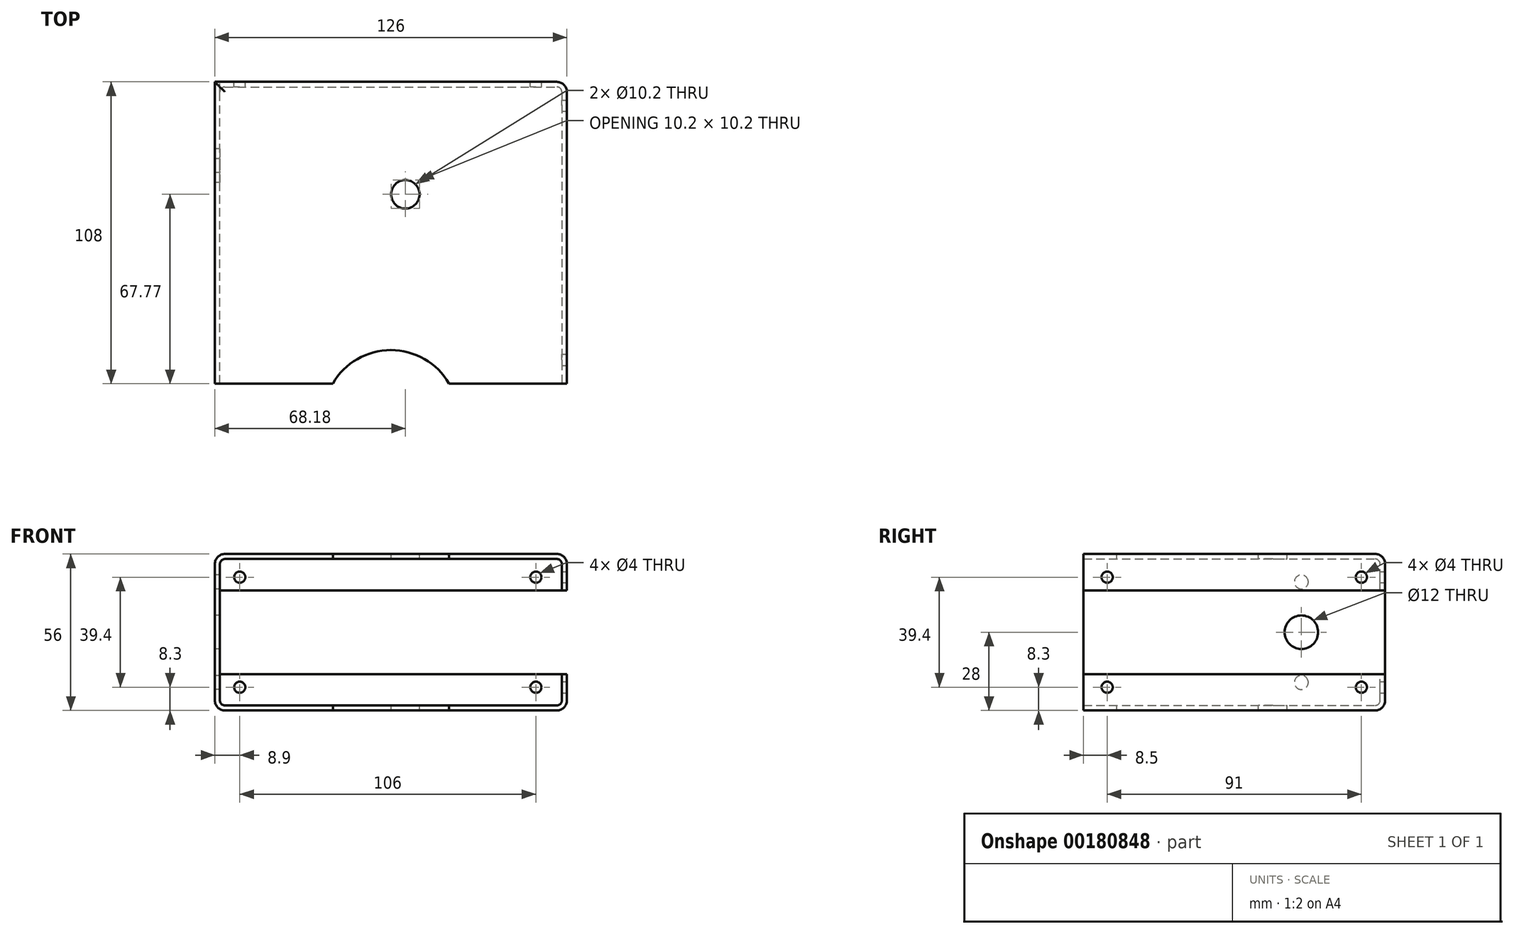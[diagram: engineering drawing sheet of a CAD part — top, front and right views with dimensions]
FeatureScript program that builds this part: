
annotation { "Feature Type Name" : "Feature", "Feature Type Description" : "" }
export const myFeature = defineFeature(function(context is Context, id is Id, definition is map)
    precondition{}
    {
        {
            var Q0;
            Q0=qCreatedBy(makeId("Front.planeOp"),FACE);
            var sketch = newSketch(context, id + "F0", { "sketchPlane" : qUnion([Q0])});
            skLineSegment(sketch, "E0.bottom", {"start": v(63, -28) * mm, "end": v(-63, -28) * mm});
            skLineSegment(sketch, "E0.top", {"start": v(63, 28) * mm, "end": v(-63, 28) * mm});
            skLineSegment(sketch, "E0.left", {"start": v(63, -28) * mm, "end": v(63, 28) * mm});
            skLineSegment(sketch, "E0.right", {"start": v(-63, -28) * mm, "end": v(-63, 28) * mm});
            skPoint(sketch, "E0.middle", {"position": v(0, 0) * mm});
            skSolve(sketch);
        }
        {
            var Q0;
            Q0 = qSketchRegion(id + "F0", true);
            extrude(context, id + "F1", {"entities" : qUnion([Q0]), "depth" : 108 * mm});
        }
        {
            var Q0;
            Q0=makeQuery(id+"F1.opExtrude","CAP_FACE",FACE,{"disambiguationData":[OSD([sQuery(id+"F0.wireOp",EDGE,"E0.bottom"),sQuery(id+"F0.wireOp",EDGE,"E0.top"),sQuery(id+"F0.wireOp",EDGE,"E0.left"),sQuery(id+"F0.wireOp",EDGE,"E0.right")])],"isStart":false});
            shell(context, id + "F2", {"entities" : qUnion([Q0]), "thickness" : 1.8 * mm});
        }
        {
            var Q0;
            {var subQ0=sQuery(id+"F0.wireOp",EDGE,"E0.right");Q0=makeQuery(id+"F2.opShell","OFFSET_EDGE",EDGE,{"disambiguationData":[OSD([subQ0]),TDD([makeQuery(id+"F1.opExtrude","CAP_EDGE",EDGE,{"disambiguationData":[OSD([subQ0])],"isStart":true})])]});}
            var Q1;
            Q1=makeQuery(id+"F2.opShell","OFFSET_EDGE",EDGE,{"disambiguationData":[OSD([sQuery(id+"F0.wireOp",EDGE,"E0.bottom"),sQuery(id+"F0.wireOp",EDGE,"E0.right")])]});
            var Q2;
            {var subQ0=sQuery(id+"F0.wireOp",EDGE,"E0.bottom");Q2=makeQuery(id+"F2.opShell","OFFSET_EDGE",EDGE,{"disambiguationData":[OSD([subQ0]),TDD([makeQuery(id+"F1.opExtrude","CAP_EDGE",EDGE,{"disambiguationData":[OSD([subQ0])],"isStart":true})])]});}
            var Q3;
            {var subQ0=sQuery(id+"F0.wireOp",EDGE,"E0.top");Q3=makeQuery(id+"F2.opShell","OFFSET_EDGE",EDGE,{"disambiguationData":[OSD([subQ0]),TDD([makeQuery(id+"F1.opExtrude","CAP_EDGE",EDGE,{"disambiguationData":[OSD([subQ0])],"isStart":true})])]});}
            var Q4;
            Q4=makeQuery(id+"F2.opShell","OFFSET_EDGE",EDGE,{"disambiguationData":[OSD([sQuery(id+"F0.wireOp",EDGE,"E0.top"),sQuery(id+"F0.wireOp",EDGE,"E0.right")])]});
            var Q5;
            {var subQ0=sQuery(id+"F0.wireOp",EDGE,"E0.left");Q5=makeQuery(id+"F2.opShell","OFFSET_EDGE",EDGE,{"disambiguationData":[OSD([subQ0]),TDD([makeQuery(id+"F1.opExtrude","CAP_EDGE",EDGE,{"disambiguationData":[OSD([subQ0])],"isStart":true})])]});}
            var Q6;
            Q6=makeQuery(id+"F2.opShell","OFFSET_EDGE",EDGE,{"disambiguationData":[OSD([sQuery(id+"F0.wireOp",EDGE,"E0.top"),sQuery(id+"F0.wireOp",EDGE,"E0.left")])]});
            var Q7;
            Q7=makeQuery(id+"F2.opShell","OFFSET_EDGE",EDGE,{"disambiguationData":[OSD([sQuery(id+"F0.wireOp",EDGE,"E0.bottom"),sQuery(id+"F0.wireOp",EDGE,"E0.left")])]});
            fillet(context, id + "F3", {"entities" : qUnion([Q0, Q1, Q2, Q3, Q4, Q5, Q6, Q7]), "radius" : 1.8 * mm, "tangentPropagation" : true, "allowEdgeOverflow" : false});
        }
        {
            var Q0;
            Q0=makeQuery(id+"F1.opExtrude","SWEPT_FACE",FACE,{"disambiguationData":[OSD([sQuery(id+"F0.wireOp",EDGE,"E0.right")])]});
            var sketch = newSketch(context, id + "F4", { "sketchPlane" : qUnion([Q0])});
            skLineSegment(sketch, "E1", {"start": v(0, 0) * mm, "end": v(30, 0) * mm});
            skCircle(sketch, "E2", {"center": v(30, 0) * mm, "radius": 6 * mm});
            skLineSegment(sketch, "E3", {"start": v(30, 0) * mm, "end": v(30, -18) * mm});
            skCircle(sketch, "E4", {"center": v(30, -18) * mm, "radius": 2.5 * mm});
            skCircle(sketch, "E5.MirrorC", {"center": v(30, 18) * mm, "radius": 2.5 * mm});
            skSolve(sketch);
        }
        {
            var Q0;
            Q0 = qSketchRegion(id + "F4", true);
            extrude(context, id + "F5", {"entities" : qUnion([Q0]), "operationType" : NewBodyOperationType.REMOVE, "oppositeDirection" : true, "depth" : 25 * mm});
        }
        {
            var Q0;
            Q0=makeQuery(id+"F1.opExtrude","CAP_FACE",FACE,{"disambiguationData":[OSD([sQuery(id+"F0.wireOp",EDGE,"E0.bottom"),sQuery(id+"F0.wireOp",EDGE,"E0.top"),sQuery(id+"F0.wireOp",EDGE,"E0.left"),sQuery(id+"F0.wireOp",EDGE,"E0.right")])],"isStart":true});
            var sketch = newSketch(context, id + "F6", { "sketchPlane" : qUnion([Q0])});
            skLineSegment(sketch, "E6", {"start": v(-63, 28) * mm, "end": v(-63, 15) * mm});
            skLineSegment(sketch, "E7", {"start": v(-63, 15) * mm, "end": v(63, 15) * mm});
            skLineSegment(sketch, "E8", {"start": v(63, 15) * mm, "end": v(63, 28) * mm});
            skLineSegment(sketch, "E9.MirrorCS", {"start": v(-63, -15) * mm, "end": v(63, -15) * mm});
            skLineSegment(sketch, "E10.MirrorCS", {"start": v(-63, -28) * mm, "end": v(-63, -15) * mm});
            skLineSegment(sketch, "E11.MirrorCS", {"start": v(63, -15) * mm, "end": v(63, -28) * mm});
            skLineSegment(sketch, "E12", {"start": v(-63, 15) * mm, "end": v(-63, -15) * mm});
            skLineSegment(sketch, "E13", {"start": v(63, 15) * mm, "end": v(63, -15) * mm});
            skLineSegment(sketch, "E14.0", {"start": v(61.2, 15) * mm, "end": v(61.2, -15) * mm});
            skSolve(sketch);
        }
        {
            var Q0;
            {var subQ0=sQuery(id+"F6.wireOp",EDGE,"E12");Q0=makeQuery(id+"F6.imprint","IMPRINT",FACE,{"disambiguationData":[TD([[makeQuery(id+"F6.imprint","IMPRINT",EDGE,{"derivedFrom":subQ0}),-1.0]])]});}
            extrude(context, id + "F7", {"entities" : qUnion([Q0]), "operationType" : NewBodyOperationType.REMOVE, "oppositeDirection" : true, "depth" : 120 * mm});
        }
        {
            var Q0;
            Q0=makeQuery(id+"F1.opExtrude","CAP_EDGE",EDGE,{"disambiguationData":[OSD([sQuery(id+"F0.wireOp",EDGE,"E0.bottom")])],"isStart":true});
            var Q1;
            Q1=makeQuery(id+"F1.opExtrude","SWEPT_EDGE",EDGE,{"disambiguationData":[OSD([sQuery(id+"F0.wireOp",EDGE,"E0.bottom"),sQuery(id+"F0.wireOp",EDGE,"E0.left")])]});
            var Q2;
            {var subQ0=sQuery(id+"F0.wireOp",EDGE,"E0.bottom");var subQ1=sQuery(id+"F0.wireOp",EDGE,"E0.left");Q2=makeQuery(id+"F7.boolean.opBoolean","SPLIT",EDGE,{"disambiguationData":[TD([makeQuery(id+"F1.opExtrude","SWEPT_FACE",FACE,{"disambiguationData":[OSD([subQ0])]})])],"derivedFrom":makeQuery(id+"F1.opExtrude","CAP_EDGE",EDGE,{"disambiguationData":[OSD([subQ1])],"isStart":true})});}
            var Q3;
            {var subQ0=sQuery(id+"F0.wireOp",EDGE,"E0.left");var subQ1=sQuery(id+"F0.wireOp",EDGE,"E0.top");Q3=makeQuery(id+"F7.boolean.opBoolean","SPLIT",EDGE,{"disambiguationData":[TD([makeQuery(id+"F1.opExtrude","SWEPT_FACE",FACE,{"disambiguationData":[OSD([subQ1])]})])],"derivedFrom":makeQuery(id+"F1.opExtrude","CAP_EDGE",EDGE,{"disambiguationData":[OSD([subQ0])],"isStart":true})});}
            var Q4;
            Q4=makeQuery(id+"F1.opExtrude","SWEPT_EDGE",EDGE,{"disambiguationData":[OSD([sQuery(id+"F0.wireOp",EDGE,"E0.top"),sQuery(id+"F0.wireOp",EDGE,"E0.left")])]});
            var Q5;
            Q5=makeQuery(id+"F1.opExtrude","CAP_EDGE",EDGE,{"disambiguationData":[OSD([sQuery(id+"F0.wireOp",EDGE,"E0.top")])],"isStart":true});
            var Q6;
            Q6=makeQuery(id+"F1.opExtrude","SWEPT_EDGE",EDGE,{"disambiguationData":[OSD([sQuery(id+"F0.wireOp",EDGE,"E0.top"),sQuery(id+"F0.wireOp",EDGE,"E0.right")])]});
            var Q7;
            Q7=makeQuery(id+"F1.opExtrude","SWEPT_EDGE",EDGE,{"disambiguationData":[OSD([sQuery(id+"F0.wireOp",EDGE,"E0.bottom"),sQuery(id+"F0.wireOp",EDGE,"E0.right")])]});
            fillet(context, id + "F8", {"entities" : qUnion([Q0, Q1, Q2, Q3, Q4, Q5, Q6, Q7]), "radius" : 3.6 * mm, "tangentPropagation" : true, "allowEdgeOverflow" : false});
        }
        {
            var Q0;
            Q0=makeQuery(id+"F1.opExtrude","SWEPT_FACE",FACE,{"disambiguationData":[OSD([sQuery(id+"F0.wireOp",EDGE,"E0.top")])]});
            var sketch = newSketch(context, id + "F9", { "sketchPlane" : qUnion([Q0])});
            skLineSegment(sketch, "E15", {"start": v(59.4, -108) * mm, "end": v(0, -108) * mm});
            skLineSegment(sketch, "E16", {"start": v(0, -96) * mm, "end": v(0, -108) * mm});
            skLineSegment(sketch, "E17", {"start": v(0, -108) * mm, "end": v(0, -120) * mm});
            skCircle(sketch, "E18", {"center": v(0, -120) * mm, "radius": 24 * mm});
            skLineSegment(sketch, "E19.0", {"start": v(5.18, -108) * mm, "end": v(5.18, -120) * mm});
            skLineSegment(sketch, "E20", {"start": v(5.18, -120) * mm, "end": v(5.18, -40.23) * mm});
            skLineSegment(sketch, "E21", {"start": v(5.18, -40.23) * mm, "end": v(3.55, -40.23) * mm});
            skCircle(sketch, "E22", {"center": v(5.18, -40.23) * mm, "radius": 5.1 * mm});
            skSolve(sketch);
        }
        {
            var Q0;
            Q0 = qSketchRegion(id + "F9", true);
            extrude(context, id + "F10", {"entities" : qUnion([Q0]), "operationType" : NewBodyOperationType.REMOVE, "oppositeDirection" : true, "depth" : 56 * mm});
        }
        {
            var Q0;
            {var subQ1=sQuery(id+"F0.wireOp",EDGE,"E0.left");var subQ2=sQuery(id+"F0.wireOp",EDGE,"E0.top");Q0=makeQuery(id+"F7.boolean.opBoolean","SPLIT",FACE,{"disambiguationData":[TD([makeQuery(id+"F1.opExtrude","SWEPT_FACE",FACE,{"disambiguationData":[OSD([subQ2])]})])],"derivedFrom":makeQuery(id+"F1.opExtrude","SWEPT_FACE",FACE,{"disambiguationData":[OSD([subQ1])]})});}
            var sketch = newSketch(context, id + "F11", { "sketchPlane" : qUnion([Q0])});
            skLineSegment(sketch, "E23", {"start": v(-108, 19.7) * mm, "end": v(-99.5, 19.7) * mm});
            skCircle(sketch, "E24", {"center": v(-99.5, 19.7) * mm, "radius": 2 * mm});
            skLineSegment(sketch, "E25", {"start": v(-99.5, 19.7) * mm, "end": v(-8.5, 19.7) * mm});
            skCircle(sketch, "E26", {"center": v(-8.5, 19.7) * mm, "radius": 2 * mm});
            skCircle(sketch, "E27.MirrorC", {"center": v(-8.5, -19.7) * mm, "radius": 2 * mm});
            skCircle(sketch, "E28.MirrorC", {"center": v(-99.5, -19.7) * mm, "radius": 2 * mm});
            skSolve(sketch);
        }
        {
            var Q0;
            Q0 = qSketchRegion(id + "F11", true);
            extrude(context, id + "F12", {"entities" : qUnion([Q0]), "operationType" : NewBodyOperationType.REMOVE, "oppositeDirection" : true, "depth" : 25 * mm});
        }
        {
            var Q0;
            Q0=makeQuery(id+"F1.opExtrude","CAP_FACE",FACE,{"disambiguationData":[OSD([sQuery(id+"F0.wireOp",EDGE,"E0.bottom"),sQuery(id+"F0.wireOp",EDGE,"E0.top"),sQuery(id+"F0.wireOp",EDGE,"E0.left"),sQuery(id+"F0.wireOp",EDGE,"E0.right")])],"isStart":true});
            var sketch = newSketch(context, id + "F13", { "sketchPlane" : qUnion([Q0])});
            skLineSegment(sketch, "E29", {"start": v(-59.4, 19.7) * mm, "end": v(-51.9, 19.7) * mm});
            skCircle(sketch, "E30", {"center": v(-51.9, 19.7) * mm, "radius": 2 * mm});
            skLineSegment(sketch, "E31", {"start": v(-51.9, 19.7) * mm, "end": v(54.1, 19.7) * mm});
            skCircle(sketch, "E32", {"center": v(54.1, 19.7) * mm, "radius": 2 * mm});
            skCircle(sketch, "E33.MirrorC", {"center": v(54.1, -19.7) * mm, "radius": 2 * mm});
            skCircle(sketch, "E34.MirrorC", {"center": v(-51.9, -19.7) * mm, "radius": 2 * mm});
            skSolve(sketch);
        }
        {
            var Q0;
            Q0 = qSketchRegion(id + "F13", true);
            extrude(context, id + "F14", {"entities" : qUnion([Q0]), "operationType" : NewBodyOperationType.REMOVE, "oppositeDirection" : true, "depth" : 25 * mm});
        }
    });
